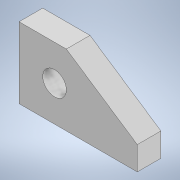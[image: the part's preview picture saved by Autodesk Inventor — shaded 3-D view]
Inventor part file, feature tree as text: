
AUTODESK INVENTOR PART (.ipt)
format: ipt  version: 2022 (Build 260153000, 153)  size: 98,304 bytes
history: native  units: mm
features: other x1, extrude x1, sketch x1
ambient origin geometry x8: Origin, YZ Plane, XZ Plane, XY Plane, X Axis, Y Axis, Z Axis, Center Point
bodies: Body1 (feature_tree)
feature tree (3):
  other  "Sólido1"
  extrude  "Extrusão1"  Depth=30.0mm
  sketch  "Esboço1"  dims[d0=50.0mm d1=30.0mm d2=20.0mm d3=10.0mm d4=10.0mm d5=15.0mm d6=15.0mm d7=10.0mm d8=0.0mm]
